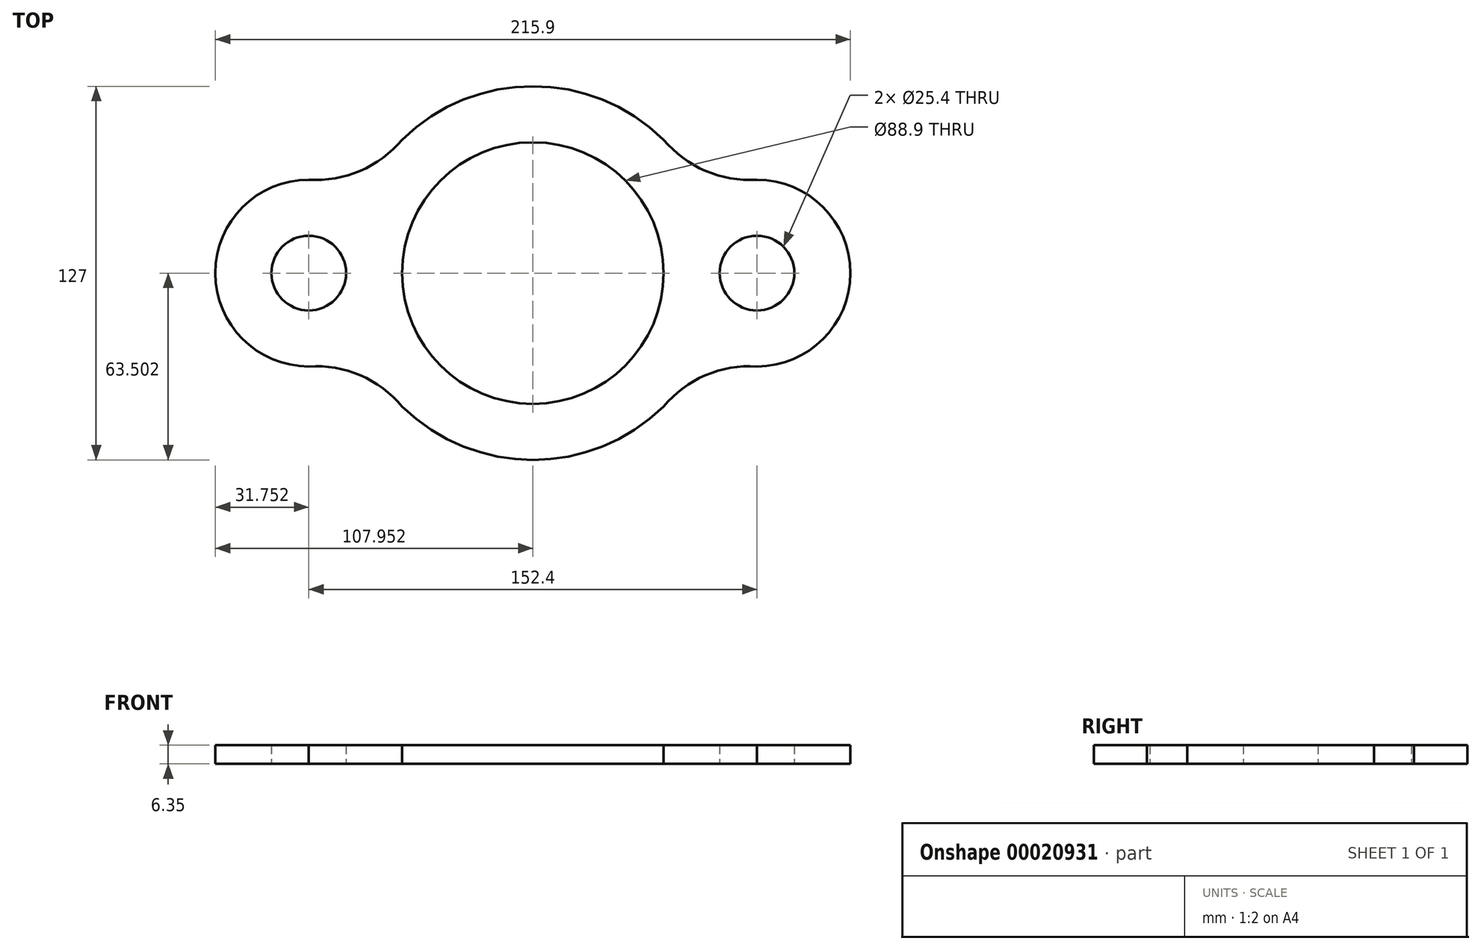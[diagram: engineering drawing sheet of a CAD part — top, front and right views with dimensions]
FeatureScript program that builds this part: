
annotation { "Feature Type Name" : "Feature", "Feature Type Description" : "" }
export const myFeature = defineFeature(function(context is Context, id is Id, definition is map)
    precondition{}
    {
        {
            var Q0;
            Q0=qCreatedBy(makeId("Top.planeOp"),FACE);
            var sketch = newSketch(context, id + "F0", { "sketchPlane" : qUnion([Q0])});
            skCircle(sketch, "E0", {"center": v(-0.36, -2.1) * mm, "radius": 44.45 * mm});
            skCircle(sketch, "E1", {"center": v(-76.56, -2.1) * mm, "radius": 12.7 * mm});
            skCircle(sketch, "E2", {"center": v(75.84, -2.1) * mm, "radius": 12.7 * mm});
            skArc(sketch, "E3", {"start": v(-48.07, -44.01) * mm, "mid": v(-0.36, -65.6) * mm, "end": v(47.35, -44.01) * mm});
            skArc(sketch, "E4", {"start": v(-74.28, 29.56) * mm, "mid": v(-108.3, -2.1) * mm, "end": v(-74.28, -33.78) * mm});
            skArc(sketch, "E5", {"start": v(73.57, -33.78) * mm, "mid": v(107.6, -2.1) * mm, "end": v(73.57, 29.56) * mm});
            skLineSegment(sketch, "E6", {"start": v(-76.56, -33.86) * mm, "end": v(-76.56, 29.64) * mm});
            skPoint(sketch, "E7.second.point", {"position": v(-44.8, -47.46) * mm});
            skPoint(sketch, "E8.second.point", {"position": v(-44.8, 43.24) * mm});
            skArc(sketch, "E9", {"start": v(-44.8, -47.46) * mm, "mid": v(-59.05, -36.85) * mm, "end": v(-76.56, -33.86) * mm});
            skArc(sketch, "E10", {"start": v(-76.56, 29.64) * mm, "mid": v(-59.05, 32.64) * mm, "end": v(-44.8, 43.24) * mm});
            skLineSegment(sketch, "E11", {"start": v(44.1, -2.1) * mm, "end": v(44.1, 43.24) * mm});
            skLineSegment(sketch, "E12", {"start": v(44.1, 43.24) * mm, "end": v(44.1, -47.46) * mm});
            skArc(sketch, "E13", {"start": v(44.1, 43.24) * mm, "mid": v(58.34, 32.64) * mm, "end": v(75.84, 29.64) * mm});
            skArc(sketch, "E14", {"start": v(75.84, -33.86) * mm, "mid": v(58.34, -36.85) * mm, "end": v(44.1, -47.46) * mm});
            skPoint(sketch, "E15.start.orphan", {"position": v(0, 61.4) * mm});
            skPoint(sketch, "E16.start.orphan", {"position": v(63.14, -2.1) * mm});
            skArc(sketch, "E17.trimOffspring", {"start": v(47.35, 39.8) * mm, "mid": v(-0.36, 61.4) * mm, "end": v(-48.07, 39.8) * mm});
            skSolve(sketch);
        }
        {
            var Q0;
            {var subQ5=sQuery(id+"F0.wireOp",EDGE,"E0");Q0=makeQuery(id+"F0.imprint","IMPRINT",FACE,{"disambiguationData":[TD([[makeQuery(id+"F0.imprint","IMPRINT",EDGE,{"derivedFrom":subQ5}),-1.0]])]});}
            var Q1;
            {var subQ0=sQuery(id+"F0.wireOp",EDGE,"E6");var subQ1=sQuery(id+"F0.wireOp",EDGE,"E1");var subQ2=makeQuery(id+"F0.imprint","INTERSECT",VERTEX,{"disambiguationData":[OD(0.0)],"derivedFrom":[subQ1,subQ0]});Q1=makeQuery(id+"F0.imprint","IMPRINT",FACE,{"disambiguationData":[TD([[makeQuery(id+"F0.imprint","IMPRINT",EDGE,{"disambiguationData":[TD([[subQ2,1.0]])],"derivedFrom":subQ1}),-1.0]])]});}
            var Q2;
            Q2=makeQuery(id+"F0.imprint","IMPRINT",FACE,{"disambiguationData":[TD([[makeQuery(id+"F0.imprint","IMPRINT",EDGE,{"derivedFrom":sQuery(id+"F0.wireOp",EDGE,"E2")}),-1.0]])]});
            extrude(context, id + "F1", {"entities" : qUnion([Q0, Q1, Q2]), "depth" : 6.35 * mm});
        }
    });
